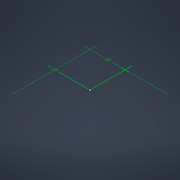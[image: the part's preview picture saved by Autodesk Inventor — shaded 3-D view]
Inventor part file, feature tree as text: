
AUTODESK INVENTOR PART (.ipt)
format: ipt  version: 2021 (Build 250183000, 183)  size: 77,824 bytes
history: native  units: mm
features: sketch x1
ambient origin geometry x8: Origin, YZ Plane, XZ Plane, XY Plane, X Axis, Y Axis, Z Axis, Center Point
feature tree (1):
  sketch  "Sketch1"  dims[d0=130.0mm d1=200.0mm]
